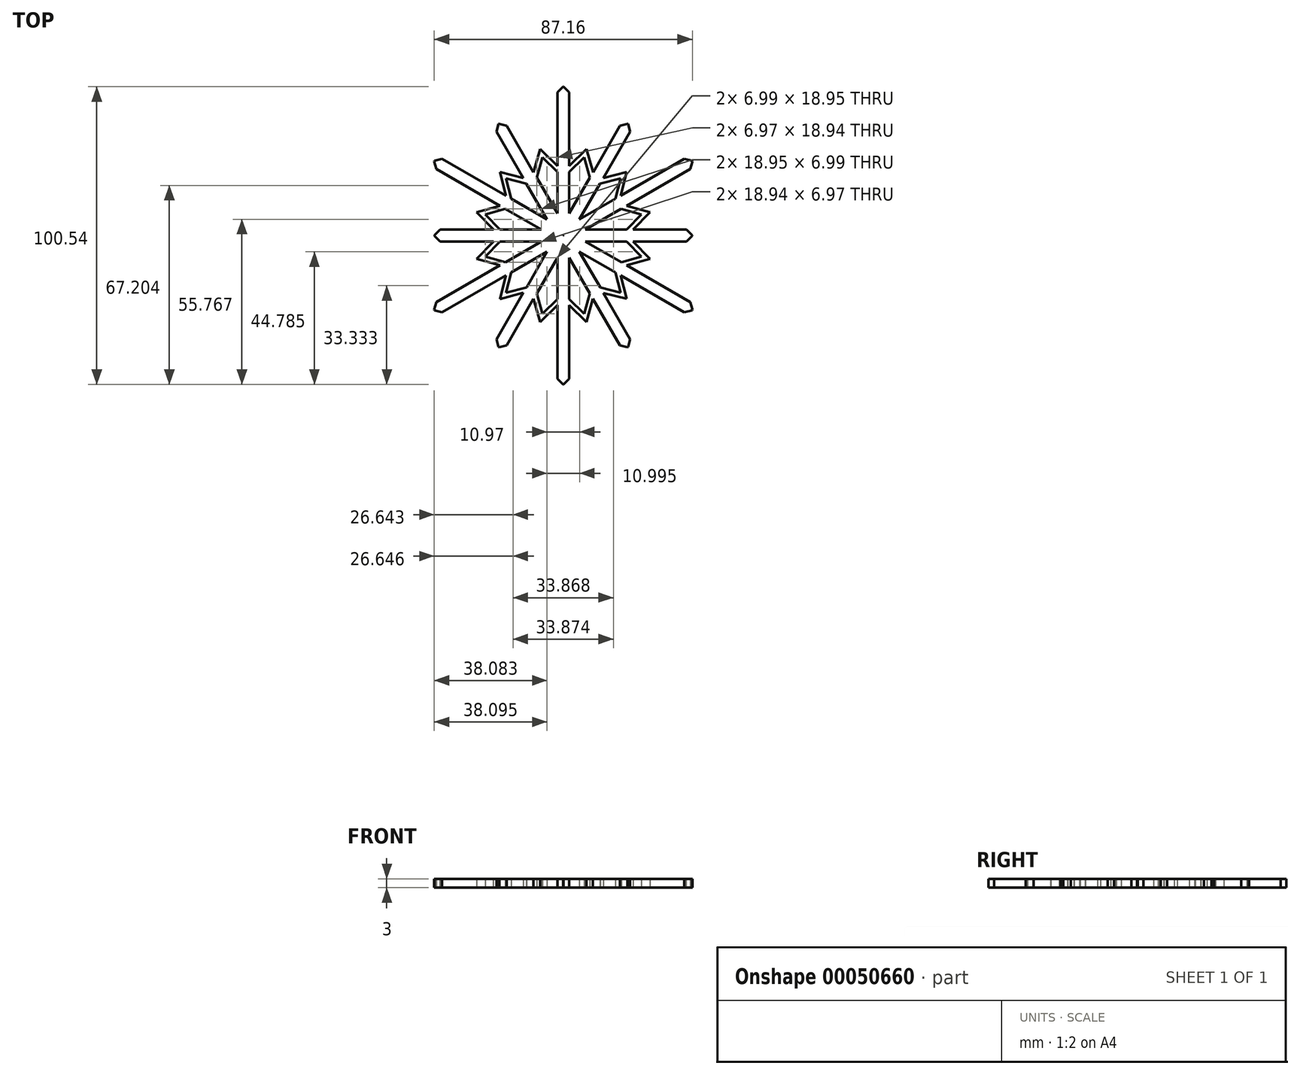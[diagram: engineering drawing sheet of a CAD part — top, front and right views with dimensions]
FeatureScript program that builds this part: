
annotation { "Feature Type Name" : "Feature", "Feature Type Description" : "" }
export const myFeature = defineFeature(function(context is Context, id is Id, definition is map)
    precondition{}
    {
        {
            var Q0;
            Q0=qCreatedBy(makeId("Top.planeOp"),FACE);
            var sketch = newSketch(context, id + "F0", { "sketchPlane" : qUnion([Q0])});
            skPoint(sketch, "E0.0.midPoint", {"position": v(21.7, 37.74) * mm});
            skLineSegment(sketch, "E1", {"start": v(-21.84, 37.66) * mm, "end": v(-5.5, 9.47) * mm});
            skLineSegment(sketch, "E2", {"start": v(43.53, 0.08) * mm, "end": v(10.95, 0.08) * mm});
            skLineSegment(sketch, "E3", {"start": v(-43.53, 0.08) * mm, "end": v(-43.53, 0.08) * mm});
            skLineSegment(sketch, "E4", {"start": v(-21.7, -37.74) * mm, "end": v(-5.46, -9.5) * mm});
            skLineSegment(sketch, "E5.bottom", {"start": v(0.05, 0.08) * mm, "end": v(-0.05, 0.08) * mm});
            skLineSegment(sketch, "E5.top", {"start": v(2, 50.27) * mm, "end": v(-2, 50.27) * mm});
            skLineSegment(sketch, "E6.trimOffspring", {"start": v(-2, 7.46) * mm, "end": v(-2, 50.27) * mm});
            skLineSegment(sketch, "E7.trimOffspring", {"start": v(2, 7.46) * mm, "end": v(2, 50.27) * mm});
            skLineSegment(sketch, "E8.trimOffspring", {"start": v(5.46, 9.5) * mm, "end": v(21.7, 37.74) * mm});
            skLineSegment(sketch, "E9.trimOffspring", {"start": v(-0.05, 0.08) * mm, "end": v(0, 0) * mm});
            skLineSegment(sketch, "E10.trimOffspring", {"start": v(0, 0) * mm, "end": v(0.05, 0.08) * mm});
            skLineSegment(sketch, "E11.trimOffspring", {"start": v(5.5, -9.47) * mm, "end": v(21.84, -37.66) * mm});
            skLineSegment(sketch, "E12.trimOffspring", {"start": v(-10.95, 0.08) * mm, "end": v(-43.53, 0.08) * mm});
            skLineSegment(sketch, "E13.1.0", {"start": v(-20.03, 38.7) * mm, "end": v(-23.5, 36.7) * mm});
            skLineSegment(sketch, "E13.1.1", {"start": v(-0.28, 4.49) * mm, "end": v(-20.03, 38.7) * mm});
            skLineSegment(sketch, "E13.1.2", {"start": v(-3.75, 2.49) * mm, "end": v(-23.5, 36.7) * mm});
            skLineSegment(sketch, "E13.2.0", {"start": v(-42.53, 26.87) * mm, "end": v(-44.53, 23.4) * mm});
            skLineSegment(sketch, "E13.2.1", {"start": v(-5.46, 5.46) * mm, "end": v(-42.53, 26.87) * mm});
            skLineSegment(sketch, "E13.2.2", {"start": v(-7.46, 2) * mm, "end": v(-44.53, 23.4) * mm});
            skLineSegment(sketch, "E13.3.0", {"start": v(-43.53, 2) * mm, "end": v(-43.53, -2) * mm});
            skLineSegment(sketch, "E13.3.1", {"start": v(-4.03, 2) * mm, "end": v(-43.53, 2) * mm});
            skLineSegment(sketch, "E13.3.2", {"start": v(-4.03, -2) * mm, "end": v(-43.53, -2) * mm});
            skLineSegment(sketch, "E13.4.0", {"start": v(-44.53, -23.4) * mm, "end": v(-42.53, -26.87) * mm});
            skLineSegment(sketch, "E13.4.1", {"start": v(-7.46, -2) * mm, "end": v(-44.53, -23.4) * mm});
            skLineSegment(sketch, "E13.4.2", {"start": v(-5.46, -5.46) * mm, "end": v(-42.53, -26.87) * mm});
            skLineSegment(sketch, "E13.5.0", {"start": v(-23.5, -36.7) * mm, "end": v(-20.03, -38.7) * mm});
            skLineSegment(sketch, "E13.5.1", {"start": v(-3.75, -2.49) * mm, "end": v(-23.5, -36.7) * mm});
            skLineSegment(sketch, "E13.5.2", {"start": v(-0.28, -4.49) * mm, "end": v(-20.03, -38.7) * mm});
            skLineSegment(sketch, "E13.6.0", {"start": v(-2, -50.27) * mm, "end": v(2, -50.27) * mm});
            skLineSegment(sketch, "E13.6.1", {"start": v(-2, -7.46) * mm, "end": v(-2, -50.27) * mm});
            skLineSegment(sketch, "E13.6.2", {"start": v(2, -7.46) * mm, "end": v(2, -50.27) * mm});
            skLineSegment(sketch, "E13.7.0", {"start": v(20.03, -38.7) * mm, "end": v(23.5, -36.7) * mm});
            skLineSegment(sketch, "E13.7.1", {"start": v(0.28, -4.49) * mm, "end": v(20.03, -38.7) * mm});
            skLineSegment(sketch, "E13.7.2", {"start": v(3.75, -2.49) * mm, "end": v(23.5, -36.7) * mm});
            skLineSegment(sketch, "E13.8.0", {"start": v(42.53, -26.87) * mm, "end": v(44.53, -23.4) * mm});
            skLineSegment(sketch, "E13.8.1", {"start": v(5.46, -5.46) * mm, "end": v(42.53, -26.87) * mm});
            skLineSegment(sketch, "E13.8.2", {"start": v(7.46, -2) * mm, "end": v(44.53, -23.4) * mm});
            skLineSegment(sketch, "E13.9.0", {"start": v(43.53, -2) * mm, "end": v(43.53, 2) * mm});
            skLineSegment(sketch, "E13.9.1", {"start": v(4.03, -2) * mm, "end": v(43.53, -2) * mm});
            skLineSegment(sketch, "E13.9.2", {"start": v(4.03, 2) * mm, "end": v(43.53, 2) * mm});
            skLineSegment(sketch, "E13.10.0", {"start": v(44.53, 23.4) * mm, "end": v(42.53, 26.87) * mm});
            skLineSegment(sketch, "E13.10.1", {"start": v(7.46, 2) * mm, "end": v(44.53, 23.4) * mm});
            skLineSegment(sketch, "E13.10.2", {"start": v(5.46, 5.46) * mm, "end": v(42.53, 26.87) * mm});
            skLineSegment(sketch, "E13.11.0", {"start": v(23.5, 36.7) * mm, "end": v(20.03, 38.7) * mm});
            skLineSegment(sketch, "E13.11.1", {"start": v(3.75, 2.49) * mm, "end": v(23.5, 36.7) * mm});
            skLineSegment(sketch, "E13.11.2", {"start": v(0.28, 4.49) * mm, "end": v(20.03, 38.7) * mm});
            skPoint(sketch, "E13.center", {"position": v(0, 0) * mm});
            skCircle(sketch, "E14", {"center": v(0, 0) * mm, "radius": 4.5 * mm});
            skLineSegment(sketch, "E15", {"start": v(-19.36, 13.49) * mm, "end": v(-21.43, 21.4) * mm});
            skLineSegment(sketch, "E16", {"start": v(-21.43, 21.4) * mm, "end": v(-13.5, 19.4) * mm});
            skLineSegment(sketch, "E17.0", {"start": v(-19.34, 19.32) * mm, "end": v(-12.46, 17.58) * mm});
            skLineSegment(sketch, "E17.1", {"start": v(-17.54, 12.43) * mm, "end": v(-19.34, 19.32) * mm});
            skLineSegment(sketch, "E18.1.0", {"start": v(-29.26, 7.82) * mm, "end": v(-21.4, 10.04) * mm});
            skLineSegment(sketch, "E18.1.1", {"start": v(-26.4, 7.06) * mm, "end": v(-19.58, 9) * mm});
            skLineSegment(sketch, "E18.1.2", {"start": v(-23.51, 2) * mm, "end": v(-29.26, 7.82) * mm});
            skLineSegment(sketch, "E18.1.3", {"start": v(-21.4, 2) * mm, "end": v(-26.4, 7.06) * mm});
            skLineSegment(sketch, "E18.2.0", {"start": v(-29.25, -7.86) * mm, "end": v(-23.55, -2) * mm});
            skLineSegment(sketch, "E18.2.1", {"start": v(-26.4, -7.09) * mm, "end": v(-21.45, -2) * mm});
            skLineSegment(sketch, "E18.2.2", {"start": v(-21.36, -10.02) * mm, "end": v(-29.25, -7.86) * mm});
            skLineSegment(sketch, "E18.2.3", {"start": v(-19.54, -8.97) * mm, "end": v(-26.4, -7.09) * mm});
            skLineSegment(sketch, "E18.3.0", {"start": v(-21.4, -21.43) * mm, "end": v(-19.4, -13.5) * mm});
            skLineSegment(sketch, "E18.3.1", {"start": v(-19.32, -19.34) * mm, "end": v(-17.58, -12.46) * mm});
            skLineSegment(sketch, "E18.3.2", {"start": v(-13.49, -19.36) * mm, "end": v(-21.4, -21.43) * mm});
            skLineSegment(sketch, "E18.3.3", {"start": v(-12.43, -17.54) * mm, "end": v(-19.32, -19.34) * mm});
            skLineSegment(sketch, "E18.4.0", {"start": v(-7.82, -29.26) * mm, "end": v(-10.04, -21.4) * mm});
            skLineSegment(sketch, "E18.4.1", {"start": v(-7.06, -26.4) * mm, "end": v(-9, -19.58) * mm});
            skLineSegment(sketch, "E18.4.2", {"start": v(-2, -23.51) * mm, "end": v(-7.82, -29.26) * mm});
            skLineSegment(sketch, "E18.4.3", {"start": v(-2, -21.4) * mm, "end": v(-7.06, -26.4) * mm});
            skLineSegment(sketch, "E18.5.0", {"start": v(7.86, -29.25) * mm, "end": v(2, -23.55) * mm});
            skLineSegment(sketch, "E18.5.1", {"start": v(7.09, -26.4) * mm, "end": v(2, -21.45) * mm});
            skLineSegment(sketch, "E18.5.2", {"start": v(10.02, -21.36) * mm, "end": v(7.86, -29.25) * mm});
            skLineSegment(sketch, "E18.5.3", {"start": v(8.97, -19.54) * mm, "end": v(7.09, -26.4) * mm});
            skLineSegment(sketch, "E18.6.0", {"start": v(21.43, -21.4) * mm, "end": v(13.5, -19.4) * mm});
            skLineSegment(sketch, "E18.6.1", {"start": v(19.34, -19.32) * mm, "end": v(12.46, -17.58) * mm});
            skLineSegment(sketch, "E18.6.2", {"start": v(19.36, -13.49) * mm, "end": v(21.43, -21.4) * mm});
            skLineSegment(sketch, "E18.6.3", {"start": v(17.54, -12.43) * mm, "end": v(19.34, -19.32) * mm});
            skLineSegment(sketch, "E18.7.0", {"start": v(29.26, -7.82) * mm, "end": v(21.4, -10.04) * mm});
            skLineSegment(sketch, "E18.7.1", {"start": v(26.4, -7.06) * mm, "end": v(19.58, -9) * mm});
            skLineSegment(sketch, "E18.7.2", {"start": v(23.51, -2) * mm, "end": v(29.26, -7.82) * mm});
            skLineSegment(sketch, "E18.7.3", {"start": v(21.4, -2) * mm, "end": v(26.4, -7.06) * mm});
            skLineSegment(sketch, "E18.8.0", {"start": v(29.25, 7.86) * mm, "end": v(23.55, 2) * mm});
            skLineSegment(sketch, "E18.8.1", {"start": v(26.4, 7.09) * mm, "end": v(21.45, 2) * mm});
            skLineSegment(sketch, "E18.8.2", {"start": v(21.36, 10.02) * mm, "end": v(29.25, 7.86) * mm});
            skLineSegment(sketch, "E18.8.3", {"start": v(19.54, 8.97) * mm, "end": v(26.4, 7.09) * mm});
            skLineSegment(sketch, "E18.9.0", {"start": v(21.4, 21.43) * mm, "end": v(19.4, 13.5) * mm});
            skLineSegment(sketch, "E18.9.1", {"start": v(19.32, 19.34) * mm, "end": v(17.58, 12.46) * mm});
            skLineSegment(sketch, "E18.9.2", {"start": v(13.49, 19.36) * mm, "end": v(21.4, 21.43) * mm});
            skLineSegment(sketch, "E18.9.3", {"start": v(12.43, 17.54) * mm, "end": v(19.32, 19.34) * mm});
            skLineSegment(sketch, "E18.10.0", {"start": v(7.82, 29.26) * mm, "end": v(10.04, 21.4) * mm});
            skLineSegment(sketch, "E18.10.1", {"start": v(7.07, 26.4) * mm, "end": v(9, 19.58) * mm});
            skLineSegment(sketch, "E18.10.2", {"start": v(2, 23.51) * mm, "end": v(7.82, 29.26) * mm});
            skLineSegment(sketch, "E18.10.3", {"start": v(2, 21.4) * mm, "end": v(7.07, 26.4) * mm});
            skLineSegment(sketch, "E18.11.0", {"start": v(-7.86, 29.25) * mm, "end": v(-2, 23.55) * mm});
            skLineSegment(sketch, "E18.11.1", {"start": v(-7.09, 26.4) * mm, "end": v(-2, 21.45) * mm});
            skLineSegment(sketch, "E18.11.2", {"start": v(-10.02, 21.36) * mm, "end": v(-7.86, 29.25) * mm});
            skLineSegment(sketch, "E18.11.3", {"start": v(-8.97, 19.54) * mm, "end": v(-7.09, 26.4) * mm});
            skSolve(sketch);
        }
        {
            var Q0;
            Q0 = qSketchRegion(id + "F0", true);
            var Q1;
            Q1=makeQuery(id+"F0.imprint","IMPRINT",FACE,{"disambiguationData":[TD([[makeQuery(id+"F0.imprint","IMPRINT",EDGE,{"derivedFrom":sQuery(id+"F0.wireOp",EDGE,"E9.trimOffspring")}),-1.0]])]});
            extrude(context, id + "F1", {"entities" : qUnion([Q0, Q1]), "depth" : 3 * mm});
        }
        {
            var Q0;
            Q0=makeQuery(id+"F1.opExtrude","SWEPT_EDGE",EDGE,{"disambiguationData":[OSD([sQuery(id+"F0.wireOp",EDGE,"E5.top"),sQuery(id+"F0.wireOp",EDGE,"E6.trimOffspring")])]});
            var Q1;
            Q1=makeQuery(id+"F1.opExtrude","SWEPT_EDGE",EDGE,{"disambiguationData":[OSD([sQuery(id+"F0.wireOp",EDGE,"E13.1.0"),sQuery(id+"F0.wireOp",EDGE,"E13.1.1")])]});
            var Q2;
            Q2=makeQuery(id+"F1.opExtrude","SWEPT_EDGE",EDGE,{"disambiguationData":[OSD([sQuery(id+"F0.wireOp",EDGE,"E13.1.0"),sQuery(id+"F0.wireOp",EDGE,"E13.1.2")])]});
            var Q3;
            Q3=makeQuery(id+"F1.opExtrude","SWEPT_EDGE",EDGE,{"disambiguationData":[OSD([sQuery(id+"F0.wireOp",EDGE,"E5.top"),sQuery(id+"F0.wireOp",EDGE,"E7.trimOffspring")])]});
            var Q4;
            Q4=makeQuery(id+"F1.opExtrude","SWEPT_EDGE",EDGE,{"disambiguationData":[OSD([sQuery(id+"F0.wireOp",EDGE,"E13.2.0"),sQuery(id+"F0.wireOp",EDGE,"E13.2.1")])]});
            var Q5;
            Q5=makeQuery(id+"F1.opExtrude","SWEPT_EDGE",EDGE,{"disambiguationData":[OSD([sQuery(id+"F0.wireOp",EDGE,"E13.2.0"),sQuery(id+"F0.wireOp",EDGE,"E13.2.2")])]});
            var Q6;
            Q6=makeQuery(id+"F1.opExtrude","SWEPT_EDGE",EDGE,{"disambiguationData":[OSD([sQuery(id+"F0.wireOp",EDGE,"E13.3.0"),sQuery(id+"F0.wireOp",EDGE,"E13.3.1")])]});
            var Q7;
            Q7=makeQuery(id+"F1.opExtrude","SWEPT_EDGE",EDGE,{"disambiguationData":[OSD([sQuery(id+"F0.wireOp",EDGE,"E13.3.0"),sQuery(id+"F0.wireOp",EDGE,"E13.3.2")])]});
            var Q8;
            Q8=makeQuery(id+"F1.opExtrude","SWEPT_EDGE",EDGE,{"disambiguationData":[OSD([sQuery(id+"F0.wireOp",EDGE,"E13.4.0"),sQuery(id+"F0.wireOp",EDGE,"E13.4.1")])]});
            var Q9;
            Q9=makeQuery(id+"F1.opExtrude","SWEPT_EDGE",EDGE,{"disambiguationData":[OSD([sQuery(id+"F0.wireOp",EDGE,"E13.11.0"),sQuery(id+"F0.wireOp",EDGE,"E13.11.2")])]});
            var Q10;
            Q10=makeQuery(id+"F1.opExtrude","SWEPT_EDGE",EDGE,{"disambiguationData":[OSD([sQuery(id+"F0.wireOp",EDGE,"E13.11.0"),sQuery(id+"F0.wireOp",EDGE,"E13.11.1")])]});
            var Q11;
            Q11=makeQuery(id+"F1.opExtrude","SWEPT_EDGE",EDGE,{"disambiguationData":[OSD([sQuery(id+"F0.wireOp",EDGE,"E13.5.0"),sQuery(id+"F0.wireOp",EDGE,"E13.5.1")])]});
            var Q12;
            Q12=makeQuery(id+"F1.opExtrude","SWEPT_EDGE",EDGE,{"disambiguationData":[OSD([sQuery(id+"F0.wireOp",EDGE,"E13.6.0"),sQuery(id+"F0.wireOp",EDGE,"E13.6.1")])]});
            var Q13;
            Q13=makeQuery(id+"F1.opExtrude","SWEPT_EDGE",EDGE,{"disambiguationData":[OSD([sQuery(id+"F0.wireOp",EDGE,"E13.8.0"),sQuery(id+"F0.wireOp",EDGE,"E13.8.1")])]});
            var Q14;
            Q14=makeQuery(id+"F1.opExtrude","SWEPT_EDGE",EDGE,{"disambiguationData":[OSD([sQuery(id+"F0.wireOp",EDGE,"E13.4.0"),sQuery(id+"F0.wireOp",EDGE,"E13.4.2")])]});
            var Q15;
            Q15=makeQuery(id+"F1.opExtrude","SWEPT_EDGE",EDGE,{"disambiguationData":[OSD([sQuery(id+"F0.wireOp",EDGE,"E13.5.0"),sQuery(id+"F0.wireOp",EDGE,"E13.5.2")])]});
            var Q16;
            Q16=makeQuery(id+"F1.opExtrude","SWEPT_EDGE",EDGE,{"disambiguationData":[OSD([sQuery(id+"F0.wireOp",EDGE,"E13.6.0"),sQuery(id+"F0.wireOp",EDGE,"E13.6.2")])]});
            var Q17;
            Q17=makeQuery(id+"F1.opExtrude","SWEPT_EDGE",EDGE,{"disambiguationData":[OSD([sQuery(id+"F0.wireOp",EDGE,"E13.7.0"),sQuery(id+"F0.wireOp",EDGE,"E13.7.1")])]});
            var Q18;
            Q18=makeQuery(id+"F1.opExtrude","SWEPT_EDGE",EDGE,{"disambiguationData":[OSD([sQuery(id+"F0.wireOp",EDGE,"E13.7.0"),sQuery(id+"F0.wireOp",EDGE,"E13.7.2")])]});
            var Q19;
            Q19=makeQuery(id+"F1.opExtrude","SWEPT_EDGE",EDGE,{"disambiguationData":[OSD([sQuery(id+"F0.wireOp",EDGE,"E13.8.0"),sQuery(id+"F0.wireOp",EDGE,"E13.8.2")])]});
            var Q20;
            Q20=makeQuery(id+"F1.opExtrude","SWEPT_EDGE",EDGE,{"disambiguationData":[OSD([sQuery(id+"F0.wireOp",EDGE,"E13.9.0"),sQuery(id+"F0.wireOp",EDGE,"E13.9.1")])]});
            var Q21;
            Q21=makeQuery(id+"F1.opExtrude","SWEPT_EDGE",EDGE,{"disambiguationData":[OSD([sQuery(id+"F0.wireOp",EDGE,"E13.9.0"),sQuery(id+"F0.wireOp",EDGE,"E13.9.2")])]});
            var Q22;
            Q22=makeQuery(id+"F1.opExtrude","SWEPT_EDGE",EDGE,{"disambiguationData":[OSD([sQuery(id+"F0.wireOp",EDGE,"E13.10.0"),sQuery(id+"F0.wireOp",EDGE,"E13.10.1")])]});
            var Q23;
            Q23=makeQuery(id+"F1.opExtrude","SWEPT_EDGE",EDGE,{"disambiguationData":[OSD([sQuery(id+"F0.wireOp",EDGE,"E13.10.0"),sQuery(id+"F0.wireOp",EDGE,"E13.10.2")])]});
            chamfer(context, id + "F2", {"entities" : qUnion([Q0, Q1, Q2, Q3, Q4, Q5, Q6, Q7, Q8, Q9, Q10, Q11, Q12, Q13, Q14, Q15, Q16, Q17, Q18, Q19, Q20, Q21, Q22, Q23]), "width" : 1.9 * mm, "tangentPropagation" : true});
        }
    });
